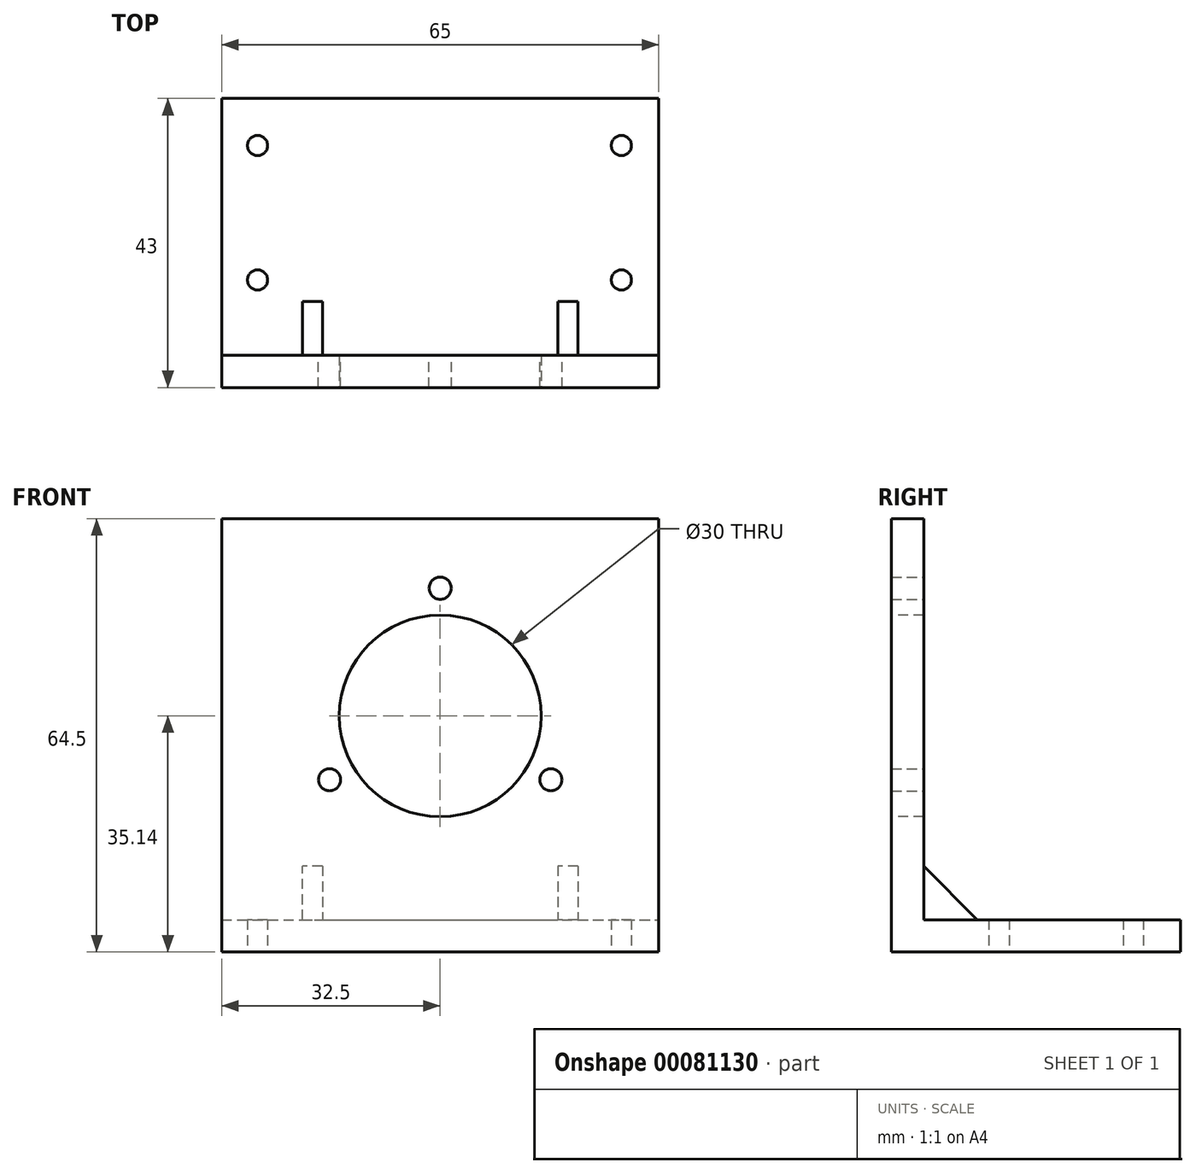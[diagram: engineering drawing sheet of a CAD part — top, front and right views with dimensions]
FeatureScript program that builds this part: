
annotation { "Feature Type Name" : "Feature", "Feature Type Description" : "" }
export const myFeature = defineFeature(function(context is Context, id is Id, definition is map)
    precondition{}
    {
        {
            var Q0;
            Q0=qCreatedBy(makeId("Top.planeOp"),FACE);
            var sketch = newSketch(context, id + "F0", { "sketchPlane" : qUnion([Q0])});
            skLineSegment(sketch, "E0.bottom", {"start": v(-32.5, 21.5) * mm, "end": v(32.5, 21.5) * mm});
            skLineSegment(sketch, "E0.top", {"start": v(-32.5, -21.5) * mm, "end": v(32.5, -21.5) * mm});
            skLineSegment(sketch, "E0.left", {"start": v(-32.5, 21.5) * mm, "end": v(-32.5, -21.5) * mm});
            skLineSegment(sketch, "E0.right", {"start": v(32.5, 21.5) * mm, "end": v(32.5, -21.5) * mm});
            skLineSegment(sketch, "E1", {"start": v(-32.5, 21.5) * mm, "end": v(32.5, -21.5) * mm, "construction": true});
            skLineSegment(sketch, "E2.bottom", {"start": v(-27.16, 14.5) * mm, "end": v(26.94, 14.5) * mm, "construction": true});
            skLineSegment(sketch, "E2.top", {"start": v(-27.16, -5.5) * mm, "end": v(26.94, -5.5) * mm, "construction": true});
            skLineSegment(sketch, "E2.left", {"start": v(-27.16, 14.5) * mm, "end": v(-27.16, -5.5) * mm, "construction": true});
            skLineSegment(sketch, "E2.right", {"start": v(26.94, 14.5) * mm, "end": v(26.94, -5.5) * mm, "construction": true});
            skCircle(sketch, "E3", {"center": v(-27.16, 14.5) * mm, "radius": 1.5 * mm});
            skCircle(sketch, "E4", {"center": v(-27.16, -5.5) * mm, "radius": 1.5 * mm});
            skCircle(sketch, "E5", {"center": v(26.94, 14.5) * mm, "radius": 1.5 * mm});
            skCircle(sketch, "E6", {"center": v(26.94, -5.5) * mm, "radius": 1.5 * mm});
            skSolve(sketch);
        }
        {
            var Q0;
            Q0=makeQuery(id+"F0.imprint","IMPRINT",FACE,{"disambiguationData":[TD([[makeQuery(id+"F0.imprint","IMPRINT",EDGE,{"derivedFrom":sQuery(id+"F0.wireOp",EDGE,"E0.bottom")}),-1.0]])]});
            extrude(context, id + "F1", {"entities" : qUnion([Q0]), "depth" : 4.8 * mm});
        }
        {
            var Q0;
            Q0=makeQuery(id+"F1.opExtrude","CAP_FACE",FACE,{"disambiguationData":[OSD([sQuery(id+"F0.wireOp",EDGE,"E0.bottom"),sQuery(id+"F0.wireOp",EDGE,"E0.top"),sQuery(id+"F0.wireOp",EDGE,"E0.left"),sQuery(id+"F0.wireOp",EDGE,"E0.right"),sQuery(id+"F0.wireOp",EDGE,"E3"),sQuery(id+"F0.wireOp",EDGE,"E4"),sQuery(id+"F0.wireOp",EDGE,"E5"),sQuery(id+"F0.wireOp",EDGE,"E6")])],"isStart":false});
            var sketch = newSketch(context, id + "F2", { "sketchPlane" : qUnion([Q0])});
            skLineSegment(sketch, "E7.bottom", {"start": v(-32.5, -16.7) * mm, "end": v(-20.5, -16.7) * mm});
            skLineSegment(sketch, "E7.top", {"start": v(-32.5, -21.5) * mm, "end": v(32.5, -21.5) * mm});
            skLineSegment(sketch, "E7.left", {"start": v(-32.5, -16.7) * mm, "end": v(-32.5, -21.5) * mm});
            skLineSegment(sketch, "E7.right", {"start": v(32.5, -16.7) * mm, "end": v(32.5, -21.5) * mm});
            skLineSegment(sketch, "E8.bottom", {"start": v(-20.5, -8.7) * mm, "end": v(-17.5, -8.7) * mm});
            skLineSegment(sketch, "E8.left", {"start": v(-20.5, -8.7) * mm, "end": v(-20.5, -16.7) * mm});
            skLineSegment(sketch, "E8.right", {"start": v(-17.5, -8.7) * mm, "end": v(-17.5, -16.7) * mm});
            skLineSegment(sketch, "E9.trimOffspring", {"start": v(-17.5, -16.7) * mm, "end": v(17.5, -16.7) * mm});
            skLineSegment(sketch, "E10", {"start": v(0, 0) * mm, "end": v(0, -27.86) * mm, "construction": true});
            skLineSegment(sketch, "E11.MirrorCS", {"start": v(17.5, -8.7) * mm, "end": v(17.5, -16.7) * mm});
            skLineSegment(sketch, "E12.MirrorCS", {"start": v(20.5, -8.7) * mm, "end": v(17.5, -8.7) * mm});
            skLineSegment(sketch, "E13.MirrorCS", {"start": v(20.5, -8.7) * mm, "end": v(20.5, -16.7) * mm});
            skLineSegment(sketch, "E14.trimOffspring", {"start": v(20.5, -16.7) * mm, "end": v(32.5, -16.7) * mm});
            skSolve(sketch);
        }
        {
            var Q0;
            Q0=makeQuery(id+"F2.imprint","IMPRINT",FACE,{"disambiguationData":[TD([[makeQuery(id+"F2.imprint","IMPRINT",EDGE,{"derivedFrom":sQuery(id+"F2.wireOp",EDGE,"E7.bottom")}),-1.0]])]});
            extrude(context, id + "F3", {"entities" : qUnion([Q0]), "operationType" : NewBodyOperationType.ADD, "depth" : 59.7 * mm});
        }
        {
            var Q0;
            Q0=makeQuery(id+"F3.opExtrude","SWEPT_FACE",FACE,{"disambiguationData":[OSD([sQuery(id+"F2.wireOp",EDGE,"E8.left")])]});
            var sketch = newSketch(context, id + "F4", { "sketchPlane" : qUnion([Q0])});
            skLineSegment(sketch, "E15", {"start": v(16.7, 64.5) * mm, "end": v(8.7, 64.5) * mm});
            skLineSegment(sketch, "E16", {"start": v(8.7, 64.5) * mm, "end": v(8.7, 4.8) * mm});
            skLineSegment(sketch, "E17", {"start": v(8.7, 4.8) * mm, "end": v(16.7, 12.8) * mm});
            skLineSegment(sketch, "E18", {"start": v(16.7, 12.8) * mm, "end": v(16.7, 64.5) * mm});
            skSolve(sketch);
        }
        {
            var Q0;
            Q0=makeQuery(id+"F4.imprint","IMPRINT",FACE,{"disambiguationData":[TD([[makeQuery(id+"F4.imprint","IMPRINT",EDGE,{"derivedFrom":sQuery(id+"F4.wireOp",EDGE,"E15")}),-1.0]])]});
            extrude(context, id + "F5", {"entities" : qUnion([Q0]), "operationType" : NewBodyOperationType.REMOVE, "endBound" : BoundingType.THROUGH_ALL, "oppositeDirection" : true, "depth" : 25 * mm});
        }
        {
            var Q0;
            Q0=makeQuery(id+"F3.boolean.opBoolean","MERGE",FACE,{"derivedFrom":[makeQuery(id+"F1.opExtrude","SWEPT_FACE",FACE,{"disambiguationData":[OSD([sQuery(id+"F0.wireOp",EDGE,"E0.top")])]}),makeQuery(id+"F3.opExtrude","SWEPT_FACE",FACE,{"disambiguationData":[OSD([sQuery(id+"F2.wireOp",EDGE,"E7.top")])]})]});
            var sketch = newSketch(context, id + "F6", { "sketchPlane" : qUnion([Q0])});
            skCircle(sketch, "E19", {"center": v(0, 35.14) * mm, "radius": 15 * mm});
            skCircle(sketch, "E20", {"center": v(0, 35.14) * mm, "radius": 19 * mm, "construction": true});
            skPoint(sketch, "E21", {"position": v(0, 54.14) * mm});
            skLineSegment(sketch, "E22", {"start": v(0, 35.14) * mm, "end": v(-16.45, 25.64) * mm, "construction": true});
            skLineSegment(sketch, "E23", {"start": v(0, 35.14) * mm, "end": v(16.45, 25.64) * mm, "construction": true});
            skSolve(sketch);
        }
        {
            var Q0;
            Q0=makeQuery(id+"F6.imprint","IMPRINT",FACE,{"disambiguationData":[TD([[makeQuery(id+"F6.imprint","IMPRINT",EDGE,{"derivedFrom":sQuery(id+"F6.wireOp",EDGE,"E19")}),1.0]])]});
            extrude(context, id + "F7", {"entities" : qUnion([Q0]), "operationType" : NewBodyOperationType.REMOVE, "endBound" : BoundingType.THROUGH_ALL, "oppositeDirection" : true, "depth" : 25 * mm});
        }
        {
            var Q0;
            Q0=sQuery(id+"F6.wireOp",VERTEX,"E21");
            var Q1;
            Q1=sQuery(id+"F6.wireOp",VERTEX,"E22.end");
            var Q2;
            Q2=sQuery(id+"F6.wireOp",VERTEX,"E23.end");
            var Q3;
            Q3=makeQuery(id+"F1.opExtrude","SWEPT_BODY",BODY,{"disambiguationData":[OSD([sQuery(id+"F0.wireOp",EDGE,"E0.bottom"),sQuery(id+"F0.wireOp",EDGE,"E0.top"),sQuery(id+"F0.wireOp",EDGE,"E0.left"),sQuery(id+"F0.wireOp",EDGE,"E0.right"),sQuery(id+"F0.wireOp",EDGE,"E3"),sQuery(id+"F0.wireOp",EDGE,"E4"),sQuery(id+"F0.wireOp",EDGE,"E5"),sQuery(id+"F0.wireOp",EDGE,"E6")])]});
            hole(context, id + "F8", {"style" : HoleStyle.SIMPLE, "endStyle" : HoleEndStyle.THROUGH, "holeDiameter" : 3.3 * mm, "startFromSketch" : true, "locations" : qUnion([Q0, Q1, Q2]), "scope" : qUnion([Q3]), "isTappedThrough" : true});
        }
    });
